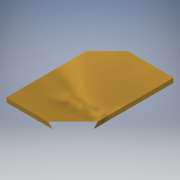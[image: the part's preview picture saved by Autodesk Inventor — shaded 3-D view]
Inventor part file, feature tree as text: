
AUTODESK INVENTOR PART (.ipt)
format: ipt  version: 2016 (Build 200138000, 138)  size: 166,912 bytes
history: native  units: mm
features: other x7, reference x5, sketch x2
ambient origin geometry x8: Origin, YZ Plane, XZ Plane, XY Plane, X Axis, Y Axis, Z Axis, Center Point
bodies: Body1 (feature_tree)
feature tree (14):
  other  "Sólido1"
  other  "Cara1"
  other  "Pestaña1"
  sketch  "Boceto1"  dims[d2=1.0mm]
  reference  "Referencia1"
  reference  "Referencia2"
  other  "Placa1"
  reference  "Referencia3"
  reference  "Referencia4"
  reference  "Referencia5"
  sketch  "Boceto2"  dims[d3=890.475mm d5=890.475mm d6=4.826mm d7=4.826mm d8=4.826mm d9=4.826mm d10=1.0mm d11=0.5mm d12=2.0mm d13=1.0mm d14=38.1mm d15=90.0deg d16=1.0mm d17=4.0mm d18=1.0mm d19=1.0mm]
  other  "Placa2"
  other  "Doblez1"
  other  "Esquina1"
